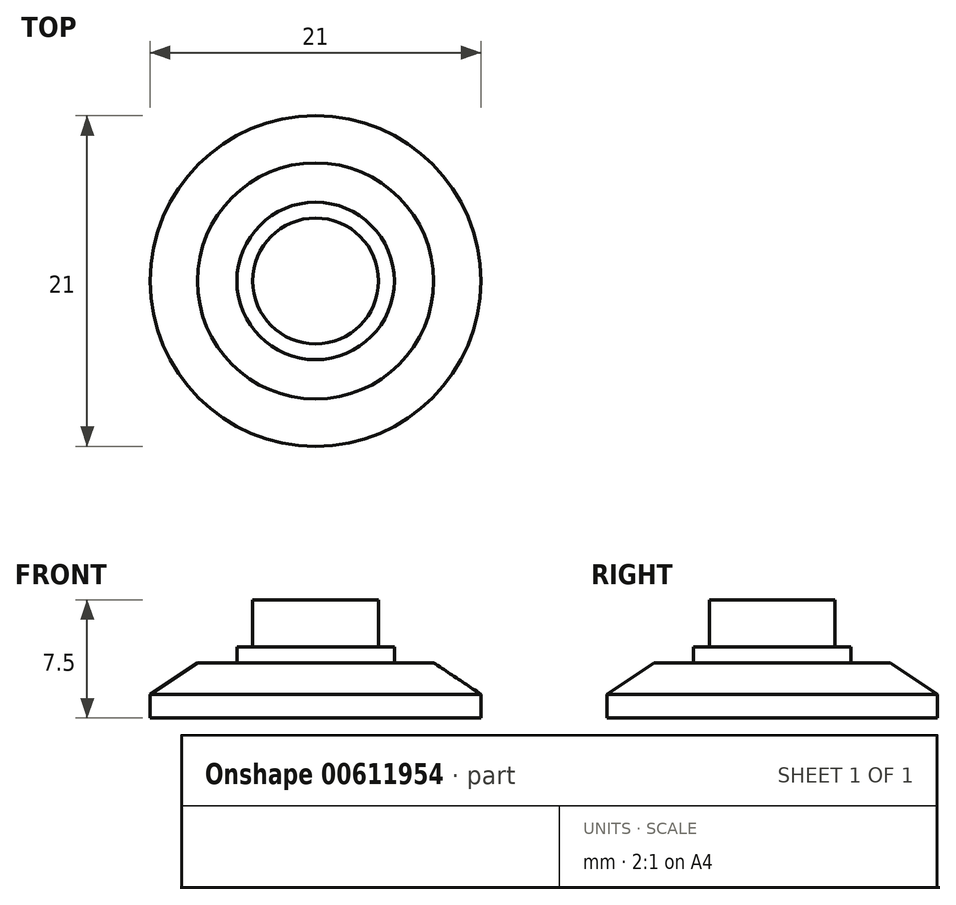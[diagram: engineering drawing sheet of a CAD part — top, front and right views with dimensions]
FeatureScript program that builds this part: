
annotation { "Feature Type Name" : "Feature", "Feature Type Description" : "" }
export const myFeature = defineFeature(function(context is Context, id is Id, definition is map)
    precondition{}
    {
        {
            var Q0;
            Q0=qCreatedBy(makeId("Top.planeOp"),FACE);
            var sketch = newSketch(context, id + "F0", { "sketchPlane" : qUnion([Q0])});
            skCircle(sketch, "E0", {"center": v(0, 0) * mm, "radius": 10.5 * mm});
            skSolve(sketch);
        }
        {
            var Q0;
            Q0 = qSketchRegion(id + "F0", true);
            extrude(context, id + "F1", {"entities" : qUnion([Q0]), "depth" : 3.5 * mm, "offsetDistance" : 25 * mm});
        }
        {
            var Q0;
            Q0=makeQuery(id+"F1.opExtrude","CAP_FACE",FACE,{"disambiguationData":[OSD([sQuery(id+"F0.wireOp",EDGE,"E0")])],"isStart":false});
            var sketch = newSketch(context, id + "F2", { "sketchPlane" : qUnion([Q0])});
            skCircle(sketch, "E1", {"center": v(0, 0) * mm, "radius": 5 * mm});
            skSolve(sketch);
        }
        {
            var Q0;
            Q0 = qSketchRegion(id + "F2", true);
            extrude(context, id + "F3", {"entities" : qUnion([Q0]), "operationType" : NewBodyOperationType.ADD, "depth" : 1 * mm, "offsetDistance" : 25 * mm});
        }
        {
            var Q0;
            Q0=makeQuery(id+"F3.opExtrude","CAP_FACE",FACE,{"disambiguationData":[OSD([sQuery(id+"F2.wireOp",EDGE,"E1")])],"isStart":false});
            var sketch = newSketch(context, id + "F4", { "sketchPlane" : qUnion([Q0])});
            skCircle(sketch, "E2", {"center": v(0, 0) * mm, "radius": 4 * mm});
            skSolve(sketch);
        }
        {
            var Q0;
            Q0 = qSketchRegion(id + "F4", true);
            extrude(context, id + "F5", {"entities" : qUnion([Q0]), "operationType" : NewBodyOperationType.ADD, "depth" : 3 * mm, "offsetDistance" : 25 * mm});
        }
        {
            var Q0;
            Q0=makeQuery(id+"F1.opExtrude","CAP_EDGE",EDGE,{"disambiguationData":[OSD([sQuery(id+"F0.wireOp",EDGE,"E0")])],"isStart":false});
            chamfer(context, id + "F6", {"entities" : qUnion([Q0]), "chamferType" : ChamferType.TWO_OFFSETS, "width1" : 3 * mm, "oppositeDirection" : false, "width2" : 2 * mm, "tangentPropagation" : true});
        }
    });
